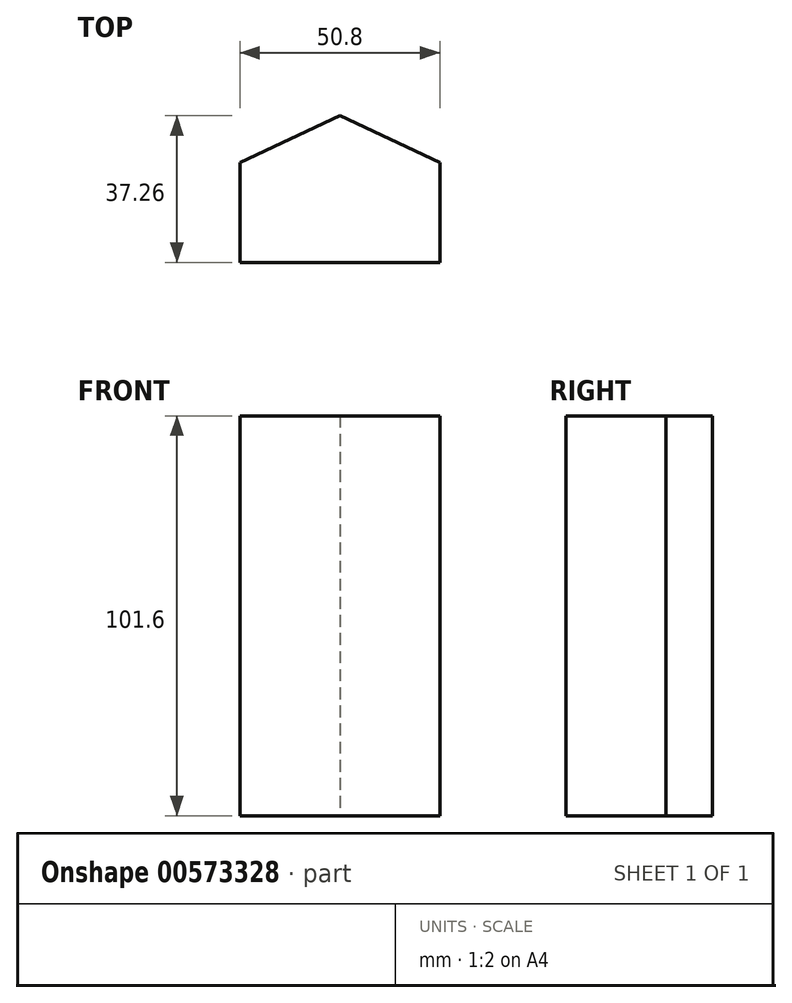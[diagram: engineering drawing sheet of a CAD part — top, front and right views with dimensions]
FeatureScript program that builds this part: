
annotation { "Feature Type Name" : "Feature", "Feature Type Description" : "" }
export const myFeature = defineFeature(function(context is Context, id is Id, definition is map)
    precondition{}
    {
        {
            var Q0;
            Q0=qCreatedBy(makeId("Top.planeOp"),FACE);
            var sketch = newSketch(context, id + "F0", { "sketchPlane" : qUnion([Q0])});
            skLineSegment(sketch, "E0.top", {"start": v(-36.03, 6.85) * mm, "end": v(14.77, 6.85) * mm});
            skLineSegment(sketch, "E0.right", {"start": v(14.77, 32.25) * mm, "end": v(14.77, 6.85) * mm});
            skPoint(sketch, "E0.middle", {"position": v(-10.63, 19.55) * mm});
            skLineSegment(sketch, "E1", {"start": v(-36.03, 32.25) * mm, "end": v(-36.03, 6.85) * mm});
            skLineSegment(sketch, "E2", {"start": v(-10.63, 44.1) * mm, "end": v(-36.03, 32.25) * mm});
            skLineSegment(sketch, "E3", {"start": v(-10.63, 44.1) * mm, "end": v(14.77, 32.25) * mm});
            skSolve(sketch);
        }
        {
            var Q0;
            Q0=makeQuery(id+"F0.imprint","IMPRINT",FACE,{"disambiguationData":[TD([[makeQuery(id+"F0.imprint","IMPRINT",EDGE,{"derivedFrom":sQuery(id+"F0.wireOp",EDGE,"E0.top")}),1.0]])]});
            extrude(context, id + "F1", {"entities" : qUnion([Q0]), "depth" : 101.6 * mm, "offsetDistance" : 25.4 * mm});
        }
    });
